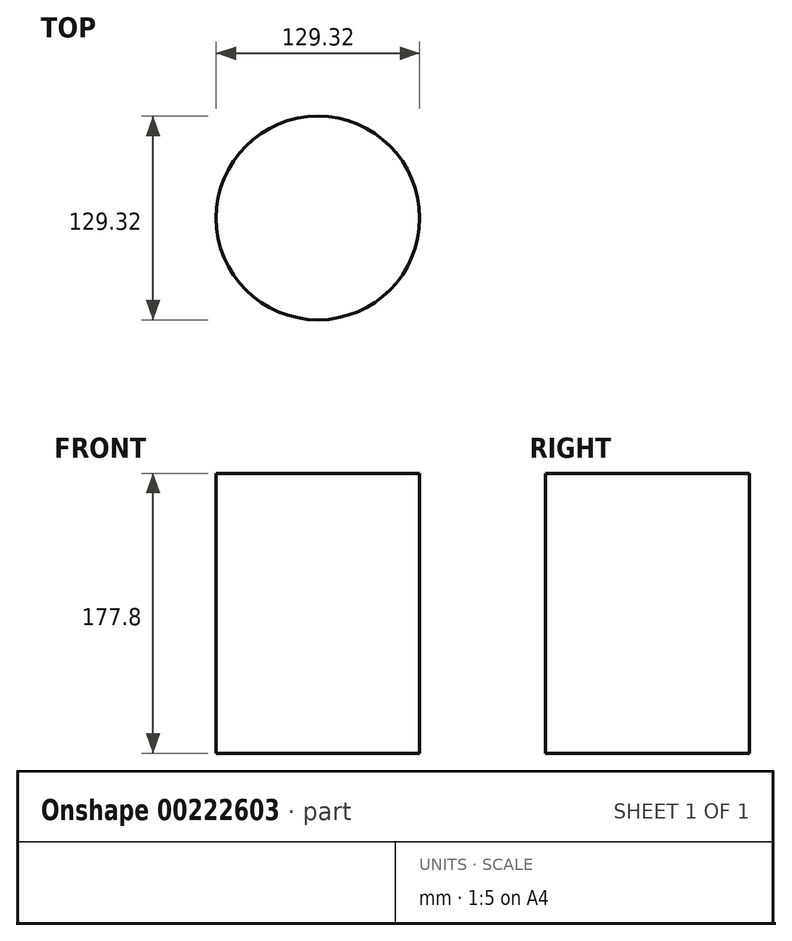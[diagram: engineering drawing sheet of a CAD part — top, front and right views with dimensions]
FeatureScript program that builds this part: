
annotation { "Feature Type Name" : "Feature", "Feature Type Description" : "" }
export const myFeature = defineFeature(function(context is Context, id is Id, definition is map)
    precondition{}
    {
        {
            var Q0;
            Q0=qCreatedBy(makeId("Top.planeOp"),FACE);
            var sketch = newSketch(context, id + "F0", { "sketchPlane" : qUnion([Q0])});
            skCircle(sketch, "E0", {"center": v(0, 0) * mm, "radius": 64.66 * mm});
            skSolve(sketch);
        }
        {
            var Q0;
            Q0=makeQuery(id+"F0.imprint","IMPRINT",FACE,{"disambiguationData":[TD([[makeQuery(id+"F0.imprint","IMPRINT",EDGE,{"derivedFrom":sQuery(id+"F0.wireOp",EDGE,"E0")}),1.0]])]});
            extrude(context, id + "F1", {"entities" : qUnion([Q0]), "endBound" : BoundingType.SYMMETRIC, "depth" : 177.8 * mm});
        }
    });
